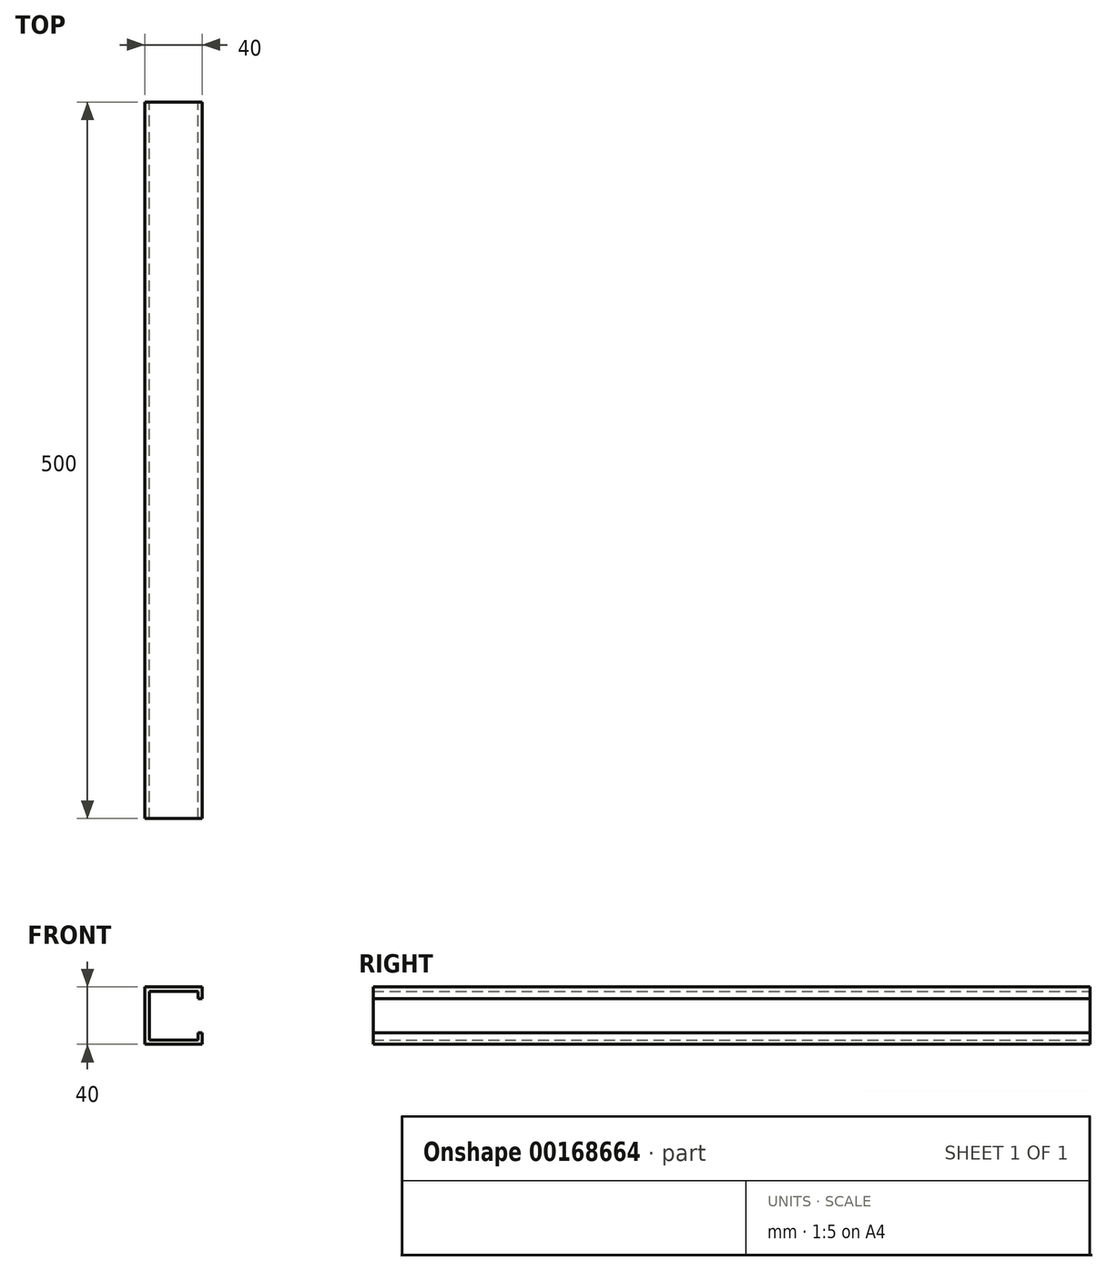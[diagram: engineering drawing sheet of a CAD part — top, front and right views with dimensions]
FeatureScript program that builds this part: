
annotation { "Feature Type Name" : "Feature", "Feature Type Description" : "" }
export const myFeature = defineFeature(function(context is Context, id is Id, definition is map)
    precondition{}
    {
        {
            var Q0;
            Q0=qCreatedBy(makeId("Front.planeOp"),FACE);
            var sketch = newSketch(context, id + "F0", { "sketchPlane" : qUnion([Q0])});
            skLineSegment(sketch, "E0.bottom", {"start": v(20, 20) * mm, "end": v(-20, 20) * mm});
            skLineSegment(sketch, "E0.top", {"start": v(20, -20) * mm, "end": v(-20, -20) * mm});
            skLineSegment(sketch, "E0.right", {"start": v(-20, 20) * mm, "end": v(-20, -20) * mm});
            skPoint(sketch, "E0.middle", {"position": v(0, 0) * mm});
            skLineSegment(sketch, "E1.0", {"start": v(17, -17) * mm, "end": v(-17, -17) * mm});
            skLineSegment(sketch, "E1.1", {"start": v(-17, 17) * mm, "end": v(-17, -17) * mm});
            skLineSegment(sketch, "E1.2", {"start": v(17, 17) * mm, "end": v(-17, 17) * mm});
            skLineSegment(sketch, "E2", {"start": v(17, 17) * mm, "end": v(17, 12) * mm});
            skLineSegment(sketch, "E3", {"start": v(17, 12) * mm, "end": v(20, 12) * mm});
            skLineSegment(sketch, "E4", {"start": v(20, -12) * mm, "end": v(17, -12) * mm});
            skLineSegment(sketch, "E5", {"start": v(17, -12) * mm, "end": v(17, -17) * mm});
            skLineSegment(sketch, "E6", {"start": v(20, 20) * mm, "end": v(20, 12) * mm});
            skLineSegment(sketch, "E7", {"start": v(20, -20) * mm, "end": v(20, -12) * mm});
            skSolve(sketch);
        }
        {
            var Q0;
            Q0=makeQuery(id+"F0.imprint","IMPRINT",FACE,{"disambiguationData":[TD([[makeQuery(id+"F0.imprint","IMPRINT",EDGE,{"derivedFrom":sQuery(id+"F0.wireOp",EDGE,"E0.bottom")}),1.0]])]});
            extrude(context, id + "F1", {"entities" : qUnion([Q0]), "depth" : 500 * mm});
        }
    });
